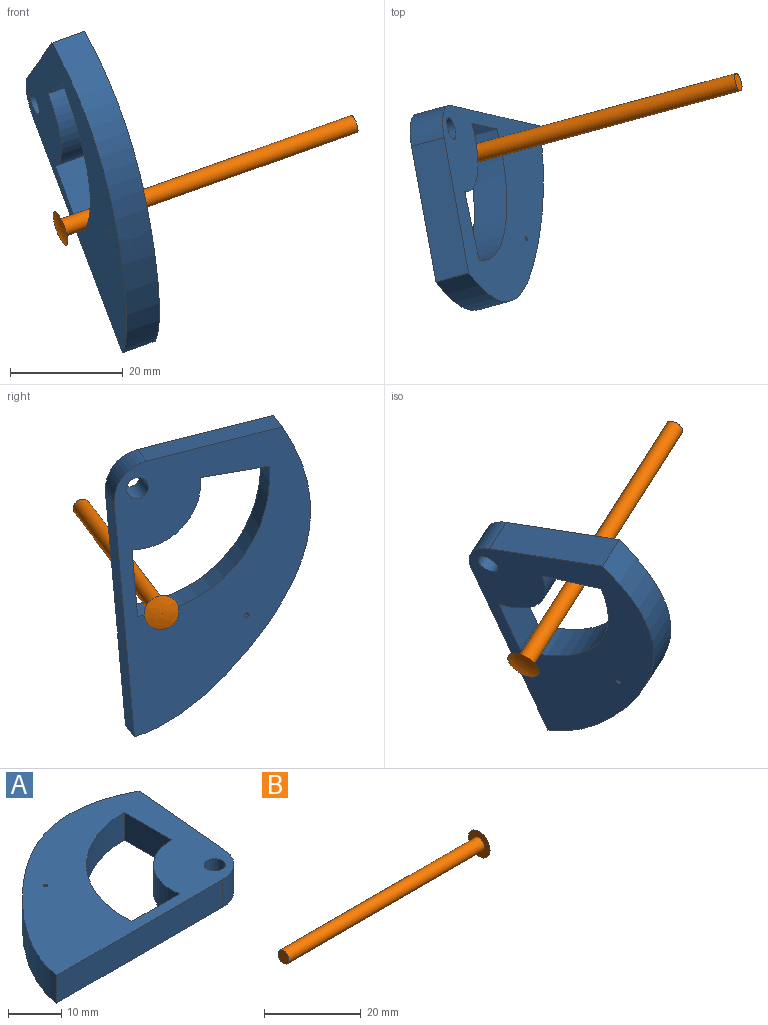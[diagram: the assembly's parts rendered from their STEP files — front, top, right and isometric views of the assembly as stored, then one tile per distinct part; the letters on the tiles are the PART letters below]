
ASSEMBLY  parts=2 mates=1
PART A: 12 faces, bbox 53.6x37.2x6.4 mm
  f0: plane 53.57x37.16mm, normal (0,0,1), area 1040.7mm2, adj f2,f3,f4,f5,f6,f7,f8,f9
  f1: plane 53.57x37.16mm, normal (0,0,-1), area 1040.7mm2, adj f2,f3,f4,f5,f6,f7,f8,f9
  f2: plane 25.11x6.35mm, normal (1,-0.09,0), area 160mm2, adj f0,f1,f3,f5
  f3: extruded ~53.57x35.56mm, area 453.5mm2, adj f0,f1,f2,f4
  f4: plane 44.25x6.35mm, normal (0,-1,0), area 281mm2, adj f0,f1,f3,f5
  f5: cylinder r=7.14mm len=7.12mm, axis (0,0,-1), area 67.3mm2, adj f0,f1,f2,f4
  f6: plane 12.71x6.35mm, normal (0,1,0), area 80.7mm2, adj f0,f1,f7,f9
  f7: cylinder r=11.56mm len=13.54mm, axis (0,0,1), area 128mm2, adj f0,f1,f6,f8
  f8: plane 12.62x6.35mm, normal (-1,0,0), area 80.1mm2, adj f0,f1,f7,f9
  f9: cylinder r=24.18mm len=26.16mm, axis (0,0,1), area 253.8mm2, adj f0,f1,f6,f8
  f10: cylinder r=1.98mm len=6.35mm, axis (0,0,1), area 79.2mm2, adj f0,f1
  f11: cylinder r=0.4mm len=6.35mm, axis (0,0,1), area 15.8mm2, adj f0,f1
PART B: 4 faces, bbox 57.5x6.4x6.4 mm
  f0: cylinder r=1.59mm len=57.15mm, axis (-1,0,0), area 570mm2, adj f1,f2
  f1: plane 3.18x3.18mm, normal (-1,0,0), area 7.9mm2, adj f0
  f2: plane 6.35x6.35mm, normal (-1,0,0), area 23.8mm2, adj f0,f3
  f3: revolved ~6.35x6.35mm, area 32.2mm2, adj f2
PLACE A rot(axis=(-0.57,-0.13,-0.81),175.6deg) t=(-39.7,-53.24,60.59)mm
PLACE B rot(axis=(0.18,-0.07,-0.98),166.8deg) t=(19.45,-48.04,53.91)mm
MATE parallel A.f1 <-> B.f0  axis (-0.91,-0.25,-0.33) through (-28.67,-70.18,42.52)mm
